# Revit family: xDrinking_Fountain-Acorn-LR1673-2-03
name_source: partatom
category: Plumbing Fixtures
units: mm (PartAtom-declared; Revit-internal decimal feet)

## family parameters
Cut with Voids When Loaded = No
Host = Face
OmniClass Number = 23.65.70.14.11
OmniClass Title = Drinking Fountains/Coolers
Part Type = Normal
Room Calculation Point = No
Round Connector Dimension = Use Diameter
Shared = Yes

## types (1)
- LR1673-2-03
    Assembly Code = D2010810
    Bowl Shape = D Shaped Bowl
    CW Connection = Yes
    CWFU = 1.5
    Cleaning and Care Guide = https://www.acorneng.com
    Conical Drinking Bubbler = Yes
    Default Elevation = 0"
    Description = Secur-Care® Ligature-Resistant, On-Floor, Wall Waste Security Drink Fountain
    Fast Drain = Yes
    Finish = Stainless Steel-Acorn-Type 304-14 Gauge-Satin
    Flow Rate = 0.7 GPM (2.65 LPM)
    HW Connection = No
    HWFU = 0
    Height 1 = 33"
    Height 2 = 32 1/2"
    Hemispherical Pushbutton = Yes
    Installation Type = Rear-Chase Mount
    Lead-Free NSF61, Section 9 & CHSC 116875 = Yes
    Length = 15 3/8"
    Manufacturer = Acorn
    Material = Stainless Steel-Acorn-Type 304-14 Gauge-Satin
    Model = LR1673-2-03
    Mounting Hardware = Yes
    Optional Cabinet -TG 12 Gage Cabinet = No
    Optional Lavatory Waste -LW1 Thru-Wall Waste Extension with P-Trap = No
    Optional Lavatory Waste -LWE Lavy Waste Extension = No
    Optional Lavatory Waste P-Trap Waste = No
    Optional Master-Trol -EVS1 Single Temp = No
    Optional Master-Trol -EVSP1 Single Temp, Piezo Button = No
    Optional Master-Trol Plus -MTP1 Single Temp = No
    Optional Master-Trol Plus -MTPP1 Single Temp, Piezo Button = No
    Optional Product -EG Enviro-Glaze = No
    Optional Product -MT Metal Template = No
    Optional Product -SW Wall Sleeve = No
    Optional Product -VAC AcornVac System = No
    Optional Programmable -PPZ1 Single Temp Programmable Piezo Button = No
    Optional Time-Trol -MVC1 Single Temp = No
    Optional Time-Trol -MVC1-BAT Single Temp Battery Powered = No
    Optional Valve -03 Single Temp, Non-Metering = No
    Optional Valve -BRS Brass Body Valve = No
    Optional Valve -MA2 Manifolded, 2-Stack = No
    Optional Valve -PFB Power Failure Bypass = No
    Optional Valve -TF Transformer, 120VAC to 24VAC = No
    Plain End Elbow Waste = Yes
    Plain End Elbow Waste Length = 3"
    Price = Prices may vary. Please consult Manufacturer Representative for most up-to-date price list.
    Product Documentation Link = https://www.acorneng.com
    Product Page URL = https://www.acorneng.com
    Required Valve Activation Force = Less than 5 lbs
    Standard Waste Outlet = Yes
    URL = https://www.acorneng.com
    Vent Connection = No
    WFU = 2
    Waste Connection = Yes
    Waste Connection Diameter = 1 1/2"
    Waste Outlet Length (Min. 3") = 3"
    Waste Outlet Option = 5 7/32"
    Width = 19"

## geometry (parser evidence)
native form markers: Sweep x2
no freeform markers — native parametric forms only
